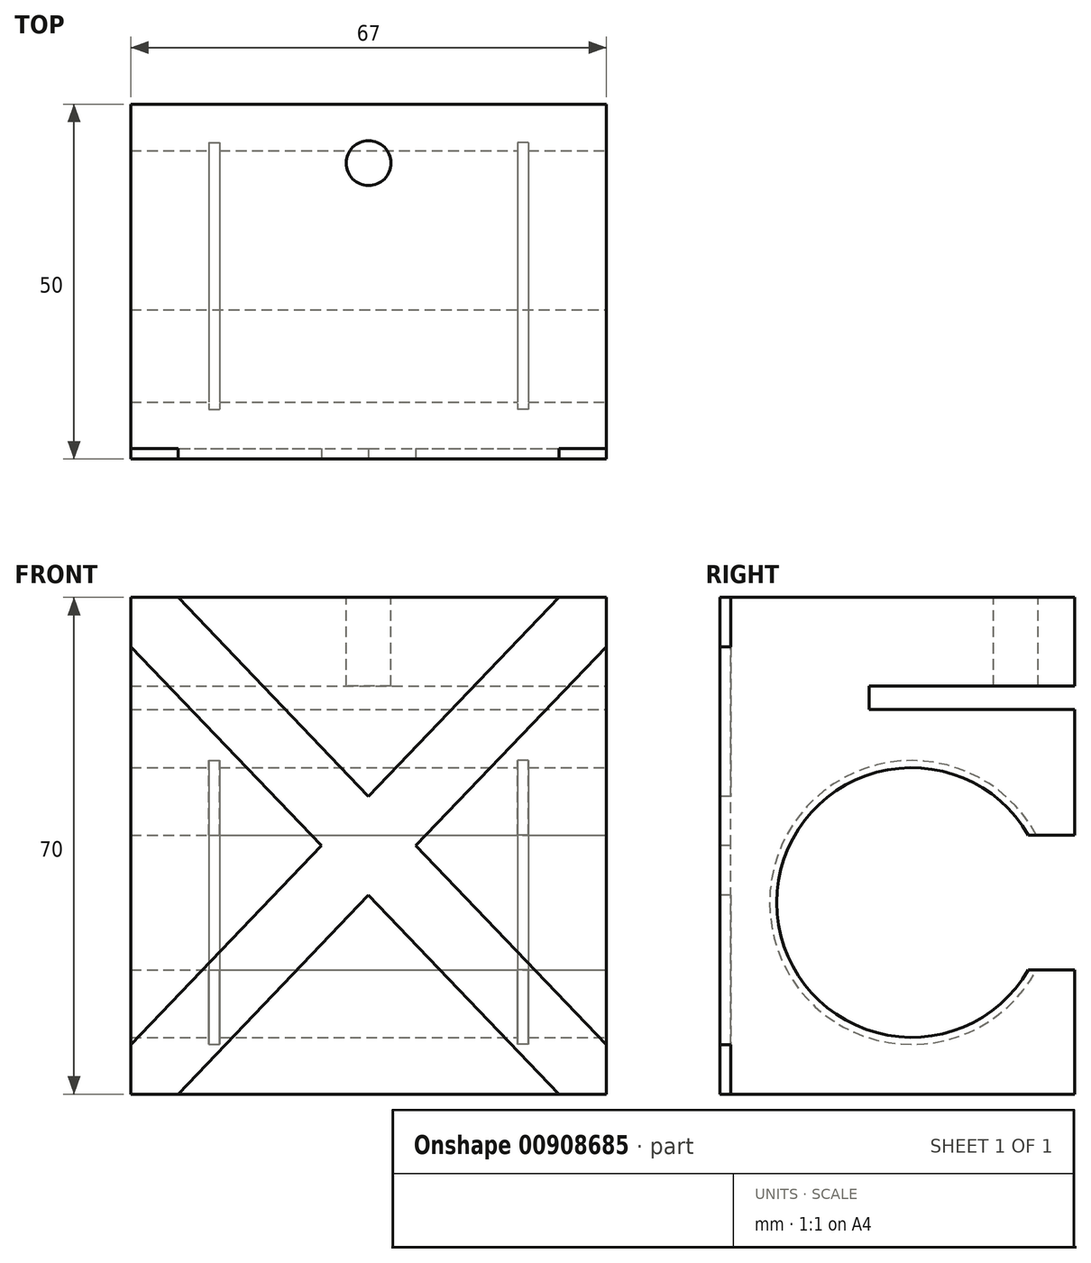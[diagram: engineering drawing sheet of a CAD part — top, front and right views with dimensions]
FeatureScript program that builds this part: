
annotation { "Feature Type Name" : "Feature", "Feature Type Description" : "" }
export const myFeature = defineFeature(function(context is Context, id is Id, definition is map)
    precondition{}
    {
        {
            var Q0;
            Q0=qCreatedBy(makeId("Right.planeOp"),FACE);
            var sketch = newSketch(context, id + "F0", { "sketchPlane" : qUnion([Q0])});
            skLineSegment(sketch, "E0.bottom", {"start": v(0, 0) * mm, "end": v(50, 0) * mm});
            skLineSegment(sketch, "E0.top", {"start": v(0, 70) * mm, "end": v(50, 70) * mm});
            skLineSegment(sketch, "E0.left", {"start": v(0, 0) * mm, "end": v(0, 70) * mm});
            skLineSegment(sketch, "E0.right", {"start": v(50, 0) * mm, "end": v(50, 70) * mm});
            skSolve(sketch);
        }
        {
            var Q0;
            Q0=makeQuery(id+"F0.imprint","IMPRINT",FACE,{"disambiguationData":[TD([[makeQuery(id+"F0.imprint","IMPRINT",EDGE,{"derivedFrom":sQuery(id+"F0.wireOp",EDGE,"E0.bottom")}),1.0]])]});
            extrude(context, id + "F1", {"entities" : qUnion([Q0]), "depth" : 67 * mm, "offsetDistance" : 25 * mm});
        }
        {
            var Q0;
            Q0=makeQuery(id+"F1.opExtrude","CAP_FACE",FACE,{"disambiguationData":[OSD([sQuery(id+"F0.wireOp",EDGE,"E0.bottom"),sQuery(id+"F0.wireOp",EDGE,"E0.top"),sQuery(id+"F0.wireOp",EDGE,"E0.left"),sQuery(id+"F0.wireOp",EDGE,"E0.right")])],"isStart":false});
            var sketch = newSketch(context, id + "F2", { "sketchPlane" : qUnion([Q0])});
            skCircle(sketch, "E1", {"center": v(27, 27) * mm, "radius": 19 * mm});
            skSolve(sketch);
        }
        {
            var Q0;
            Q0=makeQuery(id+"F2.imprint","IMPRINT",FACE,{"disambiguationData":[TD([[makeQuery(id+"F2.imprint","IMPRINT",EDGE,{"derivedFrom":sQuery(id+"F2.wireOp",EDGE,"E1")}),1.0]])]});
            extrude(context, id + "F3", {"entities" : qUnion([Q0]), "operationType" : NewBodyOperationType.REMOVE, "endBound" : BoundingType.UP_TO_NEXT, "oppositeDirection" : true, "depth" : 25 * mm, "offsetDistance" : 25 * mm});
        }
        {
            var Q0;
            Q0=makeQuery(id+"F1.opExtrude","CAP_FACE",FACE,{"disambiguationData":[OSD([sQuery(id+"F0.wireOp",EDGE,"E0.bottom"),sQuery(id+"F0.wireOp",EDGE,"E0.top"),sQuery(id+"F0.wireOp",EDGE,"E0.left"),sQuery(id+"F0.wireOp",EDGE,"E0.right")])],"isStart":false});
            cPlane(context, id + "F4", {"entities" : qUnion([Q0]), "cplaneType" : CPlaneType.OFFSET, "offset" : 12.5 * mm, "oppositeDirection" : true, "width" : 150 * mm, "height" : 150 * mm});
        }
        {
            var Q0;
            Q0=qCreatedBy(id+"F4.planeOp",FACE);
            var sketch = newSketch(context, id + "F5", { "sketchPlane" : qUnion([Q0])});
            skCircle(sketch, "E2.0", {"center": v(27, 27) * mm, "radius": 19 * mm});
            skCircle(sketch, "E3", {"center": v(27, 27) * mm, "radius": 20 * mm});
            skSolve(sketch);
        }
        {
            var Q0;
            Q0 = qSketchRegion(id + "F5", true);
            extrude(context, id + "F6", {"entities" : qUnion([Q0]), "operationType" : NewBodyOperationType.REMOVE, "depth" : 1.5 * mm, "offsetDistance" : 25 * mm});
        }
        {
            var Q0;
            Q0=qCreatedBy(id+"F4.planeOp",FACE);
            cPlane(context, id + "F7", {"entities" : qUnion([Q0]), "cplaneType" : CPlaneType.OFFSET, "offset" : 42 * mm, "oppositeDirection" : true, "width" : 150 * mm, "height" : 150 * mm});
        }
        {
            var Q0;
            Q0=qCreatedBy(id+"F7.planeOp",FACE);
            var sketch = newSketch(context, id + "F8", { "sketchPlane" : qUnion([Q0])});
            skCircle(sketch, "E4.0", {"center": v(27, 27) * mm, "radius": 19 * mm});
            skCircle(sketch, "E5", {"center": v(27, 27) * mm, "radius": 20 * mm});
            skSolve(sketch);
        }
        {
            var Q0;
            Q0 = qSketchRegion(id + "F8", true);
            extrude(context, id + "F9", {"entities" : qUnion([Q0]), "operationType" : NewBodyOperationType.REMOVE, "oppositeDirection" : true, "depth" : 1.5 * mm, "offsetDistance" : 25 * mm});
        }
        {
            var Q0;
            Q0=makeQuery(id+"F1.opExtrude","CAP_FACE",FACE,{"disambiguationData":[OSD([sQuery(id+"F0.wireOp",EDGE,"E0.bottom"),sQuery(id+"F0.wireOp",EDGE,"E0.top"),sQuery(id+"F0.wireOp",EDGE,"E0.left"),sQuery(id+"F0.wireOp",EDGE,"E0.right")])],"isStart":false});
            var sketch = newSketch(context, id + "F10", { "sketchPlane" : qUnion([Q0])});
            skLineSegment(sketch, "E6.bottom", {"start": v(50, 36.5) * mm, "end": v(40, 36.5) * mm});
            skLineSegment(sketch, "E6.top", {"start": v(50, 17.5) * mm, "end": v(40, 17.5) * mm});
            skLineSegment(sketch, "E6.left", {"start": v(50, 36.5) * mm, "end": v(50, 17.5) * mm});
            skLineSegment(sketch, "E6.right", {"start": v(40, 36.5) * mm, "end": v(40, 17.5) * mm});
            skSolve(sketch);
        }
        {
            var Q0;
            {var subQ0=sQuery(id+"F10.wireOp",EDGE,"E6.left");Q0=makeQuery(id+"F10.imprint","IMPRINT",FACE,{"disambiguationData":[TD([[makeQuery(id+"F10.imprint","IMPRINT",EDGE,{"derivedFrom":subQ0}),1.0]])]});}
            var Q1;
            Q1=makeQuery(id+"F1.opExtrude","CAP_FACE",FACE,{"disambiguationData":[OSD([sQuery(id+"F0.wireOp",EDGE,"E0.bottom"),sQuery(id+"F0.wireOp",EDGE,"E0.top"),sQuery(id+"F0.wireOp",EDGE,"E0.left"),sQuery(id+"F0.wireOp",EDGE,"E0.right")])],"isStart":true});
            extrude(context, id + "F11", {"entities" : qUnion([Q0]), "operationType" : NewBodyOperationType.REMOVE, "endBound" : BoundingType.UP_TO_SURFACE, "oppositeDirection" : true, "depth" : 25 * mm, "endBoundEntityFace" : qUnion([Q1]), "offsetDistance" : 25 * mm});
        }
        {
            var Q0;
            Q0=makeQuery(id+"F1.opExtrude","CAP_FACE",FACE,{"disambiguationData":[OSD([sQuery(id+"F0.wireOp",EDGE,"E0.bottom"),sQuery(id+"F0.wireOp",EDGE,"E0.top"),sQuery(id+"F0.wireOp",EDGE,"E0.left"),sQuery(id+"F0.wireOp",EDGE,"E0.right")])],"isStart":false});
            var sketch = newSketch(context, id + "F12", { "sketchPlane" : qUnion([Q0])});
            skLineSegment(sketch, "E7.bottom", {"start": v(50, 54.2) * mm, "end": v(21, 54.2) * mm});
            skLineSegment(sketch, "E7.top", {"start": v(50, 57.5) * mm, "end": v(21, 57.5) * mm});
            skLineSegment(sketch, "E7.left", {"start": v(50, 54.2) * mm, "end": v(50, 57.5) * mm});
            skLineSegment(sketch, "E7.right", {"start": v(21, 54.2) * mm, "end": v(21, 57.5) * mm});
            skSolve(sketch);
        }
        {
            var Q0;
            Q0 = qSketchRegion(id + "F12", true);
            extrude(context, id + "F13", {"entities" : qUnion([Q0]), "operationType" : NewBodyOperationType.REMOVE, "endBound" : BoundingType.UP_TO_NEXT, "oppositeDirection" : true, "depth" : 25 * mm, "offsetDistance" : 25 * mm});
        }
        {
            var Q0;
            Q0=makeQuery(id+"F1.opExtrude","SWEPT_FACE",FACE,{"disambiguationData":[OSD([sQuery(id+"F0.wireOp",EDGE,"E0.top")])]});
            var sketch = newSketch(context, id + "F14", { "sketchPlane" : qUnion([Q0])});
            skPoint(sketch, "E8", {"position": v(33.5, 41.7) * mm});
            skSolve(sketch);
        }
        {
            var Q0;
            Q0=sQuery(id+"F14.wireOp",VERTEX,"E8");
            var Q1;
            Q1=makeQuery(id+"F1.opExtrude","SWEPT_BODY",BODY,{"disambiguationData":[OSD([sQuery(id+"F0.wireOp",EDGE,"E0.bottom"),sQuery(id+"F0.wireOp",EDGE,"E0.top"),sQuery(id+"F0.wireOp",EDGE,"E0.left"),sQuery(id+"F0.wireOp",EDGE,"E0.right")])]});
            hole(context, id + "F15", {"style" : HoleStyle.SIMPLE, "endStyle" : HoleEndStyle.BLIND, "holeDiameter" : 6.3 * mm, "majorDiameter" : 5 * mm, "holeDepth" : 13 * mm, "isTappedThrough" : true, "tappedDepth" : 12 * mm, "tapClearance" : 3, "startFromSketch" : true, "locations" : qUnion([Q0]), "scope" : qUnion([Q1])});
        }
        {
            var Q0;
            Q0=makeQuery(id+"F1.opExtrude","SWEPT_FACE",FACE,{"disambiguationData":[OSD([sQuery(id+"F0.wireOp",EDGE,"E0.left")])]});
            var sketch = newSketch(context, id + "F16", { "sketchPlane" : qUnion([Q0])});
            skLineSegment(sketch, "E9", {"start": v(0, 70) * mm, "end": v(67, 0) * mm, "construction": true});
            skLineSegment(sketch, "E10", {"start": v(0, 0) * mm, "end": v(67, 70) * mm, "construction": true});
            skLineSegment(sketch, "E11", {"start": v(6.64, 70) * mm, "end": v(33.5, 41.94) * mm});
            skLineSegment(sketch, "E12.0", {"start": v(67, 0) * mm, "end": v(0, 0) * mm});
            skLineSegment(sketch, "E13", {"start": v(6.64, 0) * mm, "end": v(33.5, 28.06) * mm});
            skLineSegment(sketch, "E14", {"start": v(0, 6.94) * mm, "end": v(26.86, 35) * mm});
            skLineSegment(sketch, "E15", {"start": v(0, 63.06) * mm, "end": v(26.86, 35) * mm});
            skLineSegment(sketch, "E16.trimOffspring", {"start": v(40.14, 35) * mm, "end": v(67, 6.94) * mm});
            skLineSegment(sketch, "E17.trimOffspring", {"start": v(33.5, 41.94) * mm, "end": v(60.36, 70) * mm});
            skLineSegment(sketch, "E18.trimOffspring", {"start": v(33.5, 28.06) * mm, "end": v(60.36, 0) * mm});
            skLineSegment(sketch, "E19.trimOffspring", {"start": v(40.14, 35) * mm, "end": v(67, 63.06) * mm});
            skLineSegment(sketch, "E20", {"start": v(0, 63.06) * mm, "end": v(0, 70) * mm});
            skLineSegment(sketch, "E21", {"start": v(60.36, 70) * mm, "end": v(67, 70) * mm});
            skLineSegment(sketch, "E22", {"start": v(0, 6.94) * mm, "end": v(0, 0) * mm});
            skLineSegment(sketch, "E23", {"start": v(60.36, 0) * mm, "end": v(67, 0) * mm});
            skSolve(sketch);
        }
        {
            var Q0;
            {var subQ3=sQuery(id+"F16.wireOp",EDGE,"E11");Q0=makeQuery(id+"F16.imprint","IMPRINT",FACE,{"disambiguationData":[TD([[makeQuery(id+"F16.imprint","IMPRINT",EDGE,{"derivedFrom":subQ3}),-1.0]])]});}
            extrude(context, id + "F17", {"entities" : qUnion([Q0]), "operationType" : NewBodyOperationType.REMOVE, "oppositeDirection" : true, "depth" : 1.5 * mm, "offsetDistance" : 25 * mm});
        }
    });
